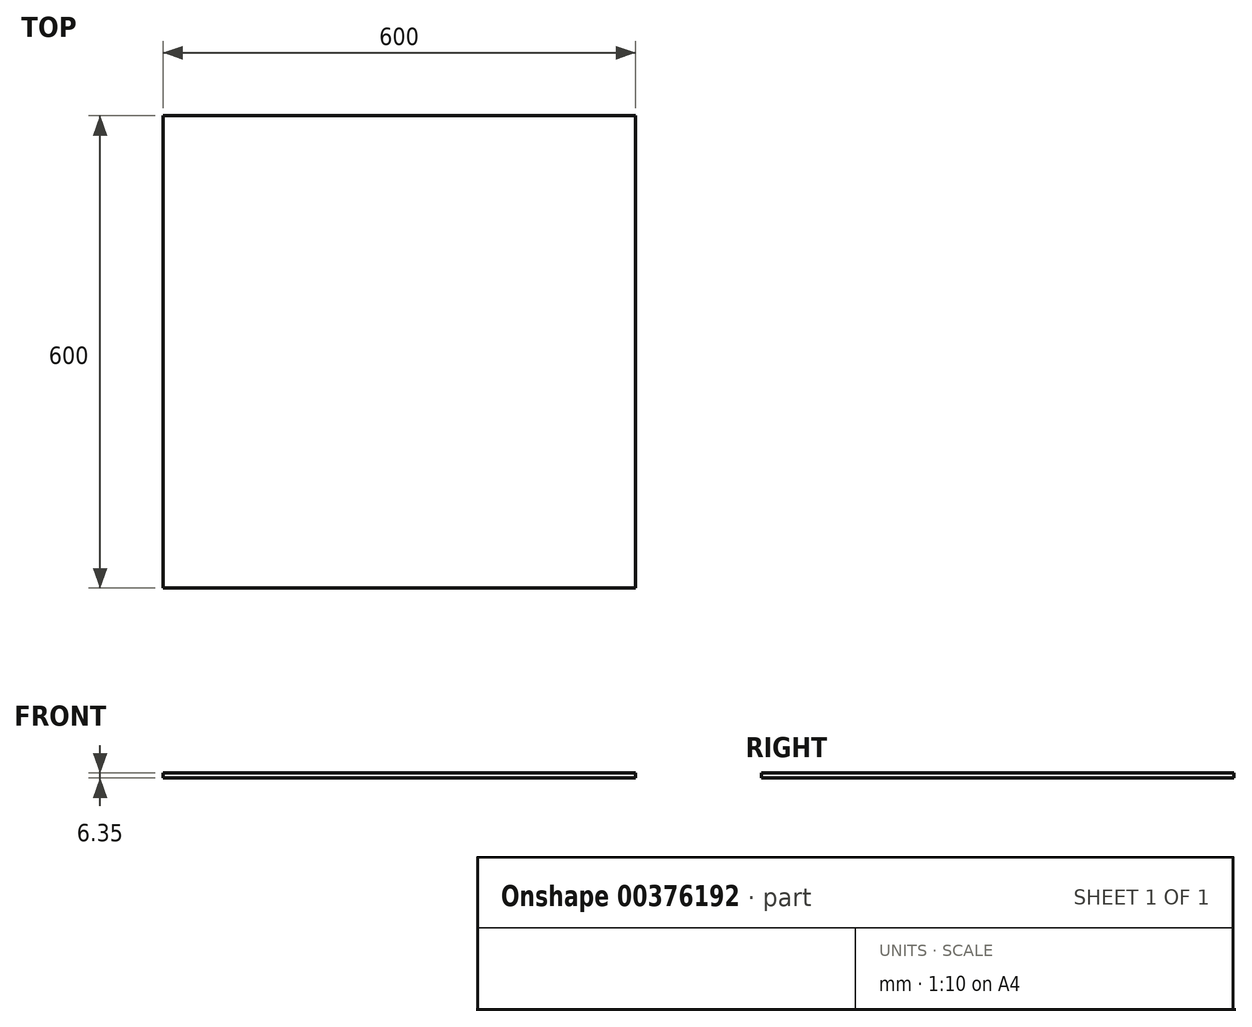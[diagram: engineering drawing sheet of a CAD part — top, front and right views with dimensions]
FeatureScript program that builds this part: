
annotation { "Feature Type Name" : "Feature", "Feature Type Description" : "" }
export const myFeature = defineFeature(function(context is Context, id is Id, definition is map)
    precondition{}
    {
        {
            var Q0;
            Q0=qCreatedBy(makeId("Top.planeOp"),FACE);
            var sketch = newSketch(context, id + "F0", { "sketchPlane" : qUnion([Q0])});
            skLineSegment(sketch, "E0.bottom", {"start": v(0, 0) * mm, "end": v(600, 0) * mm});
            skLineSegment(sketch, "E0.top", {"start": v(0, -600) * mm, "end": v(600, -600) * mm});
            skLineSegment(sketch, "E0.left", {"start": v(0, 0) * mm, "end": v(0, -600) * mm});
            skLineSegment(sketch, "E0.right", {"start": v(600, 0) * mm, "end": v(600, -600) * mm});
            skSolve(sketch);
        }
        {
            var Q0;
            Q0=makeQuery(id+"F0.imprint","IMPRINT",FACE,{"disambiguationData":[TD([[makeQuery(id+"F0.imprint","IMPRINT",EDGE,{"derivedFrom":sQuery(id+"F0.wireOp",EDGE,"E0.bottom")}),-1.0]])]});
            extrude(context, id + "F1", {"entities" : qUnion([Q0]), "depth" : 6.35 * mm});
        }
    });
